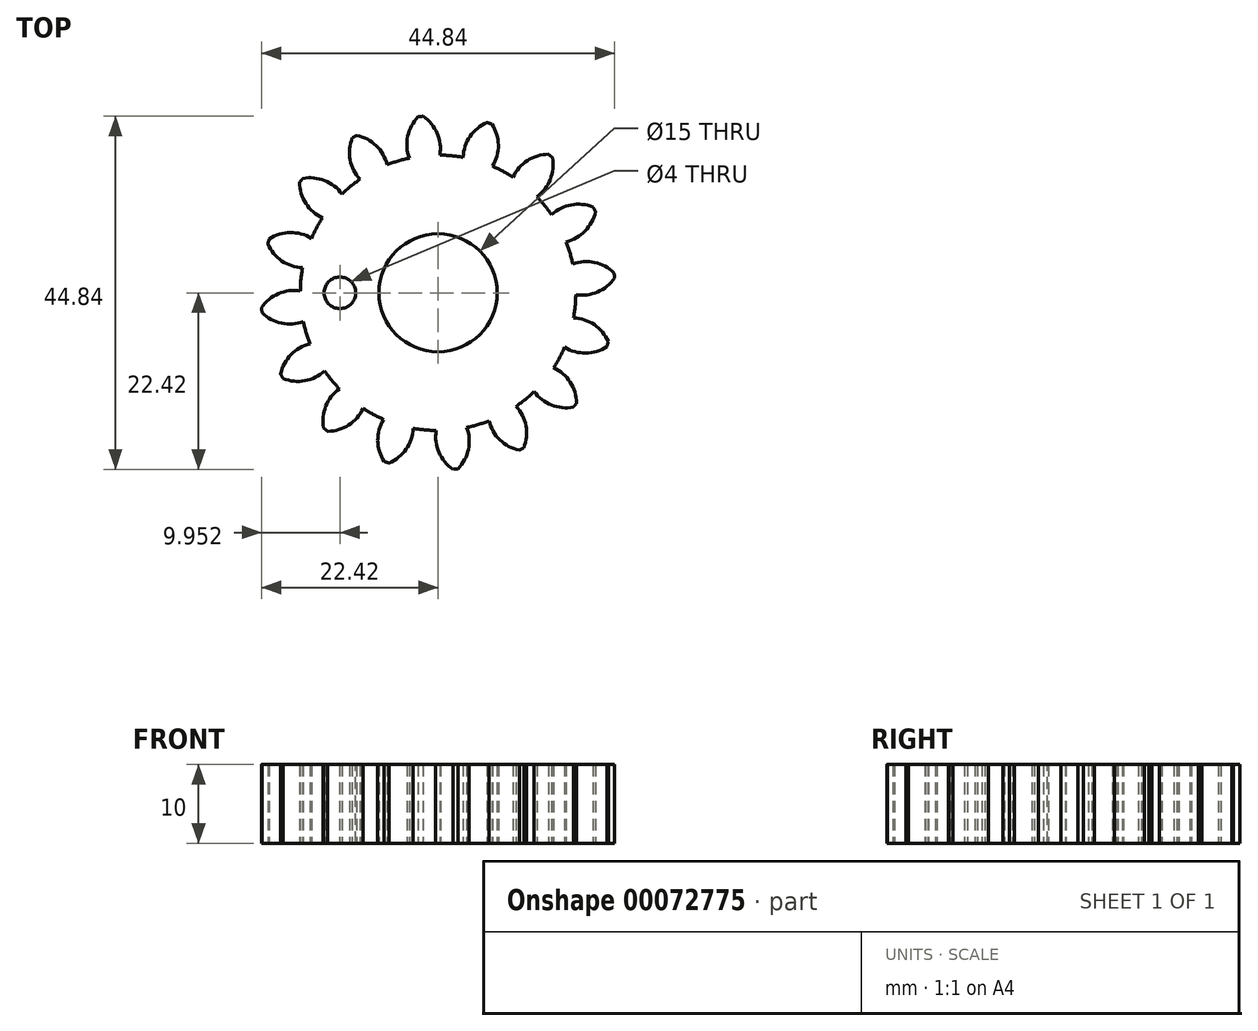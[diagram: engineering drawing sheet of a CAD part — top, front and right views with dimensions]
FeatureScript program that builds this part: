
annotation { "Feature Type Name" : "Feature", "Feature Type Description" : "" }
export const myFeature = defineFeature(function(context is Context, id is Id, definition is map)
    precondition{}
    {
        {
            var Q0;
            Q0=qCreatedBy(makeId("Top.planeOp"),FACE);
            var sketch = newSketch(context, id + "F0", { "sketchPlane" : qUnion([Q0])});
            skCircle(sketch, "E0", {"center": v(0, 0) * mm, "radius": 17.5 * mm});
            skCircle(sketch, "E1", {"center": v(0, 0) * mm, "radius": 20 * mm, "construction": true});
            skLineSegment(sketch, "E2", {"start": v(0, 0) * mm, "end": v(0, 35.23) * mm, "construction": true});
            skLineSegment(sketch, "E3", {"start": v(0, 0) * mm, "end": v(-3.6, 36.53) * mm, "construction": true});
            skLineSegment(sketch, "E4", {"start": v(0, 20) * mm, "end": v(-30.54, 20) * mm, "construction": true});
            skLineSegment(sketch, "E5", {"start": v(0, 20) * mm, "end": v(-29.66, 9.2) * mm, "construction": true});
            skCircle(sketch, "E6", {"center": v(0, 20) * mm, "radius": 5 * mm, "construction": true});
            skArc(sketch, "E7", {"start": v(-1.88, 22.42) * mm, "mid": v(-9.3, 16.31) * mm, "end": v(0.24, 17.5) * mm, "construction": true});
            skArc(sketch, "E8", {"start": v(0.24, 17.5) * mm, "mid": v(-0.1, 20.27) * mm, "end": v(-1.88, 22.42) * mm});
            skArc(sketch, "E9.MirrorCS", {"start": v(-3.65, 17.12) * mm, "mid": v(-3.85, 19.9) * mm, "end": v(-2.53, 22.36) * mm});
            skArc(sketch, "E10", {"start": v(-2.53, 22.36) * mm, "mid": v(2.2, -22.4) * mm, "end": v(-1.88, 22.42) * mm, "construction": true});
            skArc(sketch, "E11", {"start": v(-1.88, 22.42) * mm, "mid": v(-2.2, 22.4) * mm, "end": v(-2.53, 22.36) * mm});
            skCircle(sketch, "E12", {"center": v(0, 0) * mm, "radius": 7.5 * mm});
            skSolve(sketch);
        }
        {
            var Q0;
            {var subQ0=sQuery(id+"F0.wireOp",EDGE,"E0");var subQ1=makeQuery(id+"F0.imprint","INTERSECT",VERTEX,{"derivedFrom":[subQ0,sQuery(id+"F0.wireOp",EDGE,"E8")]});Q0=makeQuery(id+"F0.imprint","IMPRINT",FACE,{"disambiguationData":[TD([[makeQuery(id+"F0.imprint","IMPRINT",EDGE,{"disambiguationData":[TD([[subQ1,-1.0]])],"derivedFrom":subQ0}),1.0]])]});}
            var Q1;
            {var subQ0=sQuery(id+"F0.wireOp",EDGE,"E8");Q1=makeQuery(id+"F0.imprint","IMPRINT",FACE,{"disambiguationData":[TD([[makeQuery(id+"F0.imprint","IMPRINT",EDGE,{"derivedFrom":subQ0}),1.0]])]});}
            extrude(context, id + "F1", {"entities" : qUnion([Q0, Q1]), "depth" : 10 * mm});
        }
        {
            var Q0;
            Q0=qCreatedBy(makeId("Right.planeOp"),FACE);
            var sketch = newSketch(context, id + "F2", { "sketchPlane" : qUnion([Q0])});
            skLineSegment(sketch, "E13", {"start": v(0, 0) * mm, "end": v(0, 26.39) * mm, "construction": true});
            skSolve(sketch);
        }
        {
            var Q0;
            Q0=makeQuery(id+"F1.opExtrude","SWEPT_BODY",BODY,{"disambiguationData":[OSD([sQuery(id+"F0.wireOp",EDGE,"E0"),sQuery(id+"F0.wireOp",EDGE,"E8"),sQuery(id+"F0.wireOp",EDGE,"E9.MirrorCS"),sQuery(id+"F0.wireOp",EDGE,"E11")])]});
            var Q1;
            Q1=makeQuery(id+"F1.opExtrude","CAP_FACE",FACE,{"disambiguationData":[OSD([sQuery(id+"F0.wireOp",EDGE,"E0"),sQuery(id+"F0.wireOp",EDGE,"E8"),sQuery(id+"F0.wireOp",EDGE,"E9.MirrorCS"),sQuery(id+"F0.wireOp",EDGE,"E11")])],"isStart":false});
            var Q2;
            Q2=sQuery(id+"F2.wireOp",EDGE,"E13");
            circularPattern(context, id + "F3", {"operationType" : NewBodyOperationType.ADD, "entities" : qUnion([Q0]), "axis" : qUnion([Q2]), "angle" : 22.5 * degree, "instanceCount" : 16});
        }
        {
            var Q0;
            {var subQ0=makeQuery(id+"F1.opExtrude","CAP_FACE",FACE,{"disambiguationData":[OSD([sQuery(id+"F0.wireOp",EDGE,"E0"),sQuery(id+"F0.wireOp",EDGE,"E8"),sQuery(id+"F0.wireOp",EDGE,"E9.MirrorCS"),sQuery(id+"F0.wireOp",EDGE,"E11"),sQuery(id+"F0.wireOp",EDGE,"E12")])],"isStart":false});Q0=makeQuery(id+"F3.boolean.opBoolean","MERGE",FACE,{"derivedFrom":[subQ0,makeQuery(id+"F3.opPattern","COPY",FACE,{"derivedFrom":subQ0,"instanceName":"1"}),makeQuery(id+"F3.opPattern","COPY",FACE,{"derivedFrom":subQ0,"instanceName":"2"}),makeQuery(id+"F3.opPattern","COPY",FACE,{"derivedFrom":subQ0,"instanceName":"3"}),makeQuery(id+"F3.opPattern","COPY",FACE,{"derivedFrom":subQ0,"instanceName":"4"}),makeQuery(id+"F3.opPattern","COPY",FACE,{"derivedFrom":subQ0,"instanceName":"5"}),makeQuery(id+"F3.opPattern","COPY",FACE,{"derivedFrom":subQ0,"instanceName":"6"}),makeQuery(id+"F3.opPattern","COPY",FACE,{"derivedFrom":subQ0,"instanceName":"7"}),makeQuery(id+"F3.opPattern","COPY",FACE,{"derivedFrom":subQ0,"instanceName":"8"}),makeQuery(id+"F3.opPattern","COPY",FACE,{"derivedFrom":subQ0,"instanceName":"9"}),makeQuery(id+"F3.opPattern","COPY",FACE,{"derivedFrom":subQ0,"instanceName":"10"}),makeQuery(id+"F3.opPattern","COPY",FACE,{"derivedFrom":subQ0,"instanceName":"11"}),makeQuery(id+"F3.opPattern","COPY",FACE,{"derivedFrom":subQ0,"instanceName":"12"}),makeQuery(id+"F3.opPattern","COPY",FACE,{"derivedFrom":subQ0,"instanceName":"13"}),makeQuery(id+"F3.opPattern","COPY",FACE,{"derivedFrom":subQ0,"instanceName":"14"}),makeQuery(id+"F3.opPattern","COPY",FACE,{"derivedFrom":subQ0,"instanceName":"15"})]});}
            var sketch = newSketch(context, id + "F4", { "sketchPlane" : qUnion([Q0])});
            skCircle(sketch, "E14", {"center": v(-12.47, 0) * mm, "radius": 2 * mm});
            skSolve(sketch);
        }
        {
            var Q0;
            Q0=makeQuery(id+"F4.imprint","IMPRINT",FACE,{"disambiguationData":[TD([[makeQuery(id+"F4.imprint","IMPRINT",EDGE,{"derivedFrom":sQuery(id+"F4.wireOp",EDGE,"E14")}),1.0]])]});
            extrude(context, id + "F5", {"entities" : qUnion([Q0]), "operationType" : NewBodyOperationType.REMOVE, "oppositeDirection" : true, "depth" : 10 * mm});
        }
    });
